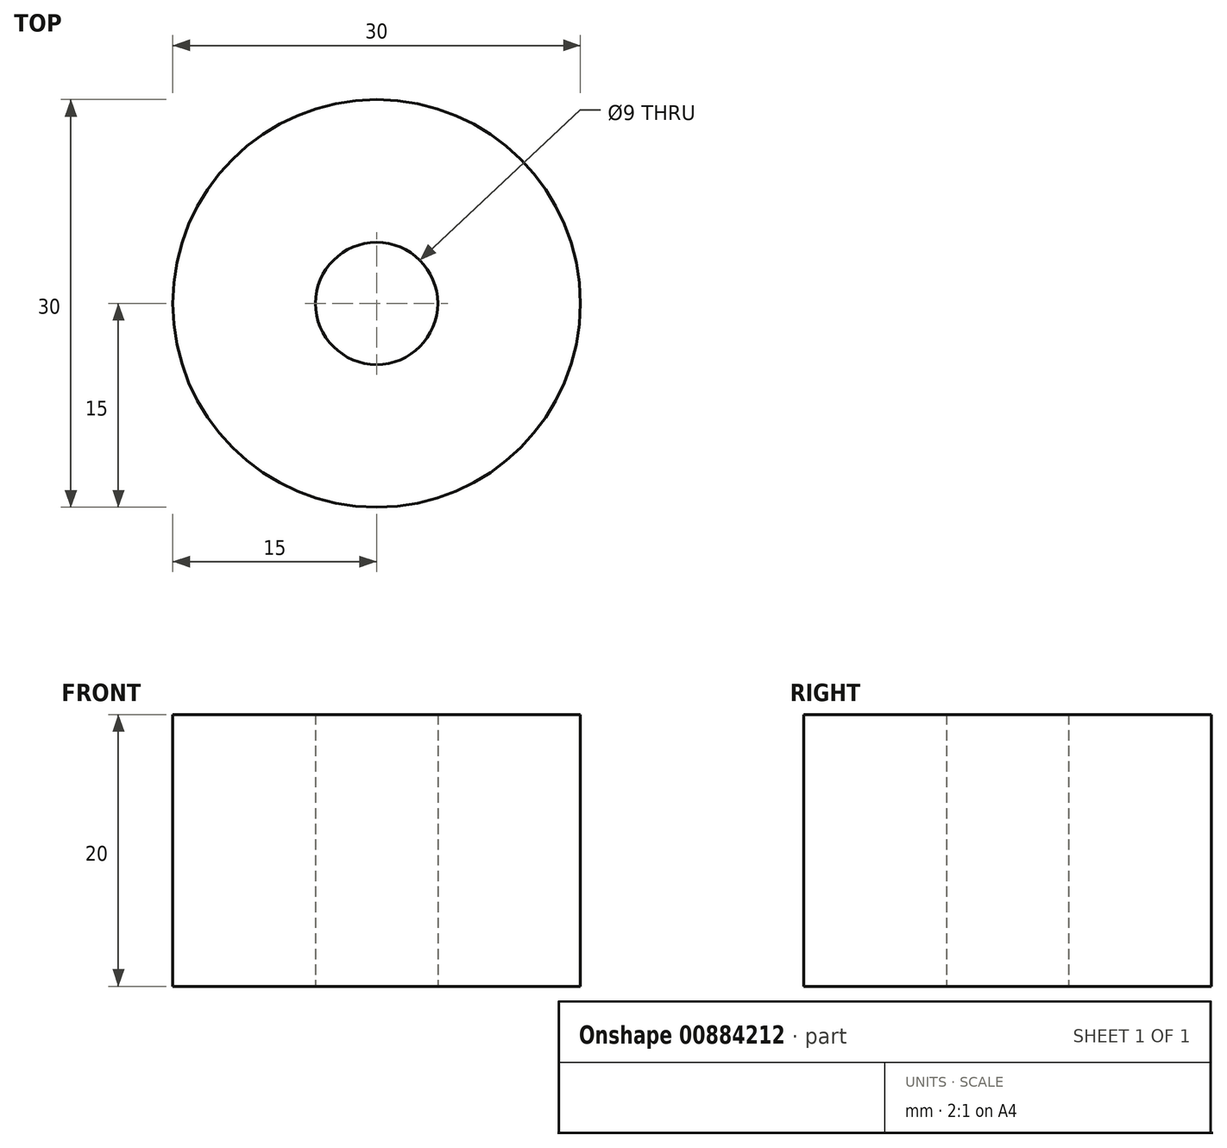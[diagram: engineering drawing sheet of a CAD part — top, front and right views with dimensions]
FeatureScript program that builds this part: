
annotation { "Feature Type Name" : "Feature", "Feature Type Description" : "" }
export const myFeature = defineFeature(function(context is Context, id is Id, definition is map)
    precondition{}
    {
        {
            var Q0;
            Q0=qCreatedBy(makeId("Top.planeOp"),FACE);
            var sketch = newSketch(context, id + "F0", { "sketchPlane" : qUnion([Q0])});
            skCircle(sketch, "E0", {"center": v(0, 0) * mm, "radius": 15 * mm});
            skCircle(sketch, "E1", {"center": v(0, 0) * mm, "radius": 4.5 * mm});
            skSolve(sketch);
        }
        {
            var Q0;
            Q0=makeQuery(id+"F0.imprint","IMPRINT",FACE,{"disambiguationData":[TD([[makeQuery(id+"F0.imprint","IMPRINT",EDGE,{"derivedFrom":sQuery(id+"F0.wireOp",EDGE,"E0")}),1.0]])]});
            extrude(context, id + "F1", {"entities" : qUnion([Q0]), "depth" : 20 * mm, "offsetDistance" : 25 * mm});
        }
    });
